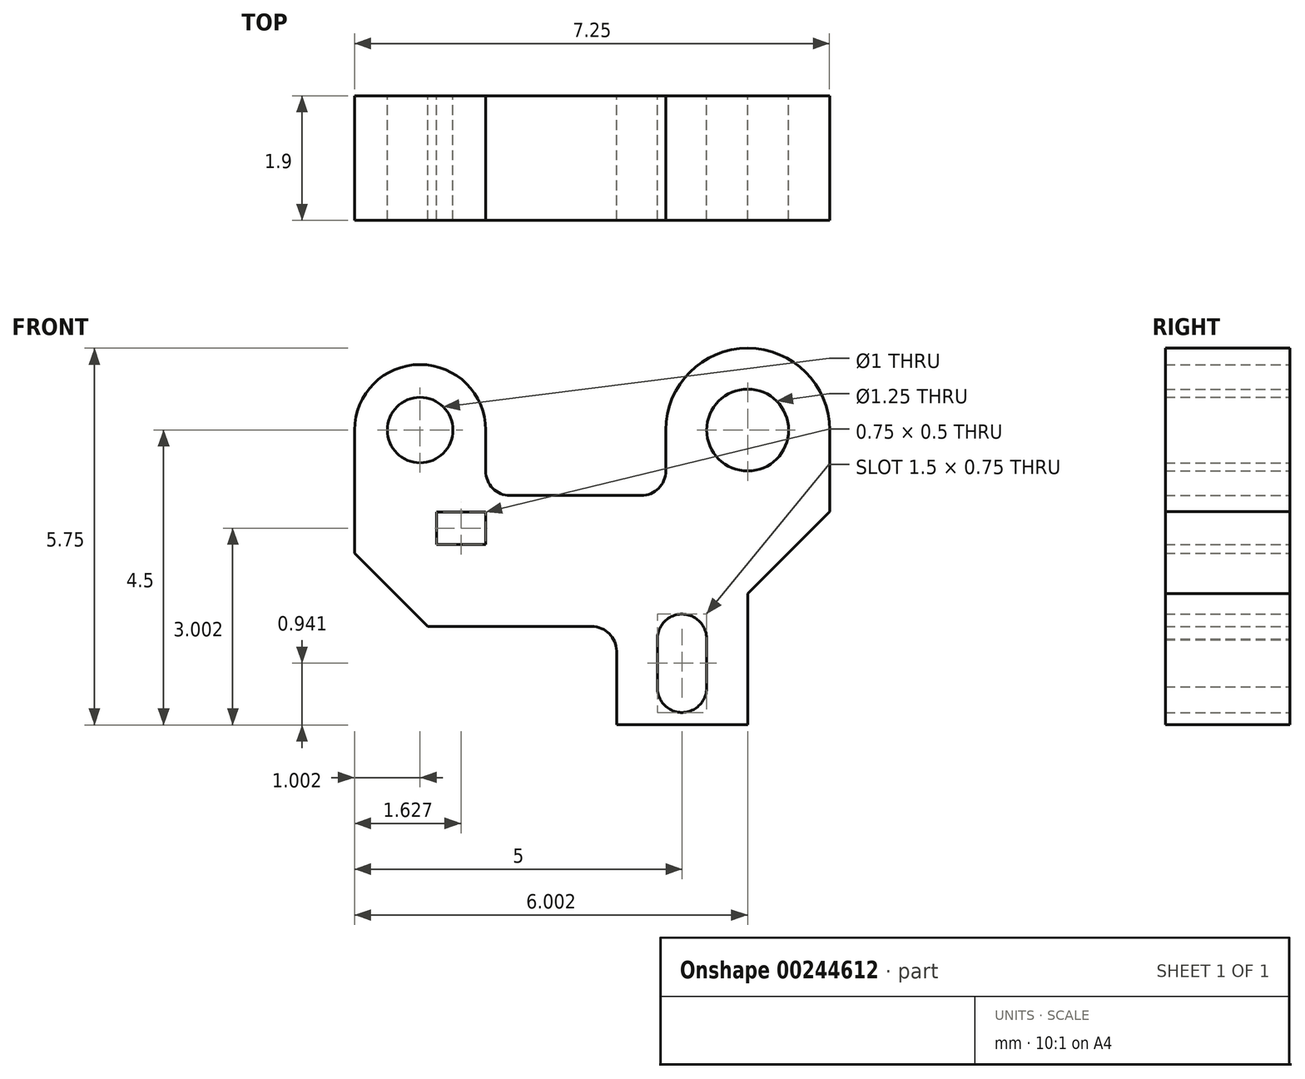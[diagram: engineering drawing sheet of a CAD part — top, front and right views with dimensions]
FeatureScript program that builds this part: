
annotation { "Feature Type Name" : "Feature", "Feature Type Description" : "" }
export const myFeature = defineFeature(function(context is Context, id is Id, definition is map)
    precondition{}
    {
        {
            var Q0;
            Q0=qCreatedBy(makeId("Front.planeOp"),FACE);
            var sketch = newSketch(context, id + "F0", { "sketchPlane" : qUnion([Q0])});
            skLineSegment(sketch, "E0.bottom", {"start": v(1.12, 0) * mm, "end": v(3.62, 0) * mm});
            skLineSegment(sketch, "E0.left", {"start": v(0, 1.12) * mm, "end": v(0, 3) * mm});
            skLineSegment(sketch, "E1", {"start": v(1.12, 0) * mm, "end": v(0, 1.12) * mm});
            skArc(sketch, "E2", {"start": v(2, 3) * mm, "mid": v(1, 4) * mm, "end": v(0, 3) * mm});
            skCircle(sketch, "E3", {"center": v(1, 3) * mm, "radius": 0.5 * mm});
            skLineSegment(sketch, "E4.bottom", {"start": v(1.25, 1.75) * mm, "end": v(2, 1.75) * mm});
            skLineSegment(sketch, "E4.top", {"start": v(1.25, 1.25) * mm, "end": v(2, 1.25) * mm});
            skLineSegment(sketch, "E4.left", {"start": v(1.25, 1.75) * mm, "end": v(1.25, 1.25) * mm});
            skLineSegment(sketch, "E4.right", {"start": v(2, 1.75) * mm, "end": v(2, 1.25) * mm});
            skLineSegment(sketch, "E5.top", {"start": v(2.38, 2) * mm, "end": v(4.38, 2) * mm});
            skLineSegment(sketch, "E5.left", {"start": v(2, 3) * mm, "end": v(2, 2.37) * mm});
            skLineSegment(sketch, "E5.right", {"start": v(4.75, 3) * mm, "end": v(4.75, 2.38) * mm});
            skLineSegment(sketch, "E6", {"start": v(6, 0.5) * mm, "end": v(6, -1.5) * mm});
            skLineSegment(sketch, "E7", {"start": v(6, -1.5) * mm, "end": v(4, -1.5) * mm});
            skLineSegment(sketch, "E8", {"start": v(4, -1.5) * mm, "end": v(4, -0.37) * mm});
            skLineSegment(sketch, "E9", {"start": v(6, 0.5) * mm, "end": v(7.25, 1.76) * mm});
            skLineSegment(sketch, "E10", {"start": v(7.25, 1.76) * mm, "end": v(7.25, 3) * mm});
            skArc(sketch, "E11", {"start": v(4.63, -0.93) * mm, "mid": v(5, -1.3) * mm, "end": v(5.37, -0.92) * mm});
            skCircle(sketch, "E12", {"center": v(6, 3) * mm, "radius": 0.62 * mm});
            skArc(sketch, "E13", {"start": v(5.37, -0.2) * mm, "mid": v(5, 0.2) * mm, "end": v(4.63, -0.2) * mm});
            skLineSegment(sketch, "E14", {"start": v(5.37, -0.2) * mm, "end": v(5.37, -0.95) * mm});
            skLineSegment(sketch, "E15", {"start": v(4.63, -0.2) * mm, "end": v(4.63, -0.93) * mm});
            skArc(sketch, "E16", {"start": v(7.25, 3) * mm, "mid": v(6, 4.25) * mm, "end": v(4.75, 3) * mm});
            skPoint(sketch, "E17.visualSharp", {"position": v(2, 2) * mm});
            skArc(sketch, "E17.filletArc", {"start": v(2, 2.37) * mm, "mid": v(2.11, 2.1) * mm, "end": v(2.38, 2) * mm});
            skPoint(sketch, "E18.visualSharp", {"position": v(4.75, 2) * mm});
            skArc(sketch, "E18.filletArc", {"start": v(4.38, 2) * mm, "mid": v(4.64, 2.1) * mm, "end": v(4.75, 2.38) * mm});
            skPoint(sketch, "E19.visualSharp", {"position": v(4, 0) * mm});
            skArc(sketch, "E19.filletArc", {"start": v(4, -0.37) * mm, "mid": v(3.9, -0.1) * mm, "end": v(3.62, 0) * mm});
            skSolve(sketch);
        }
        {
            var Q0;
            Q0=makeQuery(id+"F0.imprint","IMPRINT",FACE,{"disambiguationData":[TD([[makeQuery(id+"F0.imprint","IMPRINT",EDGE,{"derivedFrom":sQuery(id+"F0.wireOp",EDGE,"E0.bottom")}),1.0]])]});
            extrude(context, id + "F1", {"entities" : qUnion([Q0]), "depth" : 1.9 * mm});
        }
    });
